# Revit family: vanity unit for handrinse basin, door hinge
name_source: partatom
category: Furniture
units: mm (PartAtom-declared; Revit-internal decimal feet)

## family parameters
Always vertical = Yes
Cut with Voids When Loaded = No
OmniClass Number = 23.45.00.00
OmniClass Title = Sanitary, Laundry, and Cleaning Equipment
Room Calculation Point = No
Shared = Yes
Work Plane-Based = No

## types (48) — shared parameters
BIMOBJECT = Sanitary: Compound units
CATALOG = Hansgrohe
DESIGN = Germany
ETIM = EC011381 | Bathroom furniture set
IFC = Furnishing element
L = 340
MASTERFORMAT = 12 35 30.23 | Bathroom Casework
Manufacturer = Hansgrohe
NBSYN = $BASENUMBER.-$ARTNR.-$OBERFLAECHE.-$SURFACE.-$LODLEVEL.
NN = Vanity Unit for handrinse basin, door hinge
OBJECTTYPE = Object (single object)
OMNICLASS = 23-21 19 15 33 13 | Residential Bathroom Specialty Casework
PRODUCTFAMILY = Xelu Q
PRODUCTGROUP = vanity unit
PRODUCTURL = https://pro.hansgrohe.com
REGIONSET = Worldwide
UNICLASS2015 = Pr_40_30_78_05 | Bathroom furniture
UNICLASS_2015_CODE = 40_30_78_05
UNIFORMATII = E2010 | Fixed Furnishings
UNSPSC = 56 | Furniture and Furnishings
WEIGHT = 9.9
etim7_EC011381 = EC011381

## per-type parameters (varying)
| type | ARTNR | BASENUMBER | GTINCODE | LINA | LODLEVEL | Model | NAME | NB | OBERFLAECHE | PERMALINK | SURFACE |
| Vanity unit 340_245 for handrinse basin, door hinge left-54011000-High Gloss White-CHROME-200 | 54011000 | Vanity unit 340/245 for handrinse basin, door hinge left | 4059625455135 | Vanity unit 340/245 for handrinse basin, door hinge left-54011000-High Gloss White-CHROME-200 | 200 | Vanity unit 340/245 for handrinse basin, door hinge left-54011000-High Gloss White-CHROME-200 | Xelu Q Vanity unit High Gloss White 340/245 for handrinse basin, door hinge left | Vanity unit 340/245 for handrinse basin, door hinge left-54011000-High Gloss White-CHROME-200 | High Gloss White | 54011XXX | CHROME |
| Vanity unit 340_245 for handrinse basin, door hinge left-54011000-High Gloss White-CHROME-400 | 54011000 | Vanity unit 340/245 for handrinse basin, door hinge left | 4059625455135 | Vanity unit 340/245 for handrinse basin, door hinge left-54011000-High Gloss White-CHROME-400 | 400 | Vanity unit 340/245 for handrinse basin, door hinge left-54011000-High Gloss White-CHROME-400 | Xelu Q Vanity unit High Gloss White 340/245 for handrinse basin, door hinge left | Vanity unit 340/245 for handrinse basin, door hinge left-54011000-High Gloss White-CHROME-400 | High Gloss White | 54011XXX | CHROME |
| Vanity unit 340_245 for handrinse basin, door hinge left-54011670-High Gloss White-MATT_BLACK-200 | 54011670 | Vanity unit 340/245 for handrinse basin, door hinge left | 4059625455135 | Vanity unit 340/245 for handrinse basin, door hinge left-54011670-High Gloss White-MATT_BLACK-200 | 200 | Vanity unit 340/245 for handrinse basin, door hinge left-54011670-High Gloss White-MATT_BLACK-200 | Xelu Q Vanity unit High Gloss White 340/245 for handrinse basin, door hinge left | Vanity unit 340/245 for handrinse basin, door hinge left-54011670-High Gloss White-MATT_BLACK-200 | High Gloss White | 54011XXX | MATT_BLACK |
| Vanity unit 340_245 for handrinse basin, door hinge left-54011670-High Gloss White-MATT_BLACK-400 | 54011670 | Vanity unit 340/245 for handrinse basin, door hinge left | 4059625455135 | Vanity unit 340/245 for handrinse basin, door hinge left-54011670-High Gloss White-MATT_BLACK-400 | 400 | Vanity unit 340/245 for handrinse basin, door hinge left-54011670-High Gloss White-MATT_BLACK-400 | Xelu Q Vanity unit High Gloss White 340/245 for handrinse basin, door hinge left | Vanity unit 340/245 for handrinse basin, door hinge left-54011670-High Gloss White-MATT_BLACK-400 | High Gloss White | 54011XXX | MATT_BLACK |
| Vanity unit 340_245 for handrinse basin, door hinge left-54011700-High Gloss White-MATT_WHITE-200 | 54011700 | Vanity unit 340/245 for handrinse basin, door hinge left | 4059625455135 | Vanity unit 340/245 for handrinse basin, door hinge left-54011700-High Gloss White-MATT_WHITE-200 | 200 | Vanity unit 340/245 for handrinse basin, door hinge left-54011700-High Gloss White-MATT_WHITE-200 | Xelu Q Vanity unit High Gloss White 340/245 for handrinse basin, door hinge left | Vanity unit 340/245 for handrinse basin, door hinge left-54011700-High Gloss White-MATT_WHITE-200 | High Gloss White | 54011XXX | MATT_WHITE |
| Vanity unit 340_245 for handrinse basin, door hinge left-54011700-High Gloss White-MATT_WHITE-400 | 54011700 | Vanity unit 340/245 for handrinse basin, door hinge left | 4059625455135 | Vanity unit 340/245 for handrinse basin, door hinge left-54011700-High Gloss White-MATT_WHITE-400 | 400 | Vanity unit 340/245 for handrinse basin, door hinge left-54011700-High Gloss White-MATT_WHITE-400 | Xelu Q Vanity unit High Gloss White 340/245 for handrinse basin, door hinge left | Vanity unit 340/245 for handrinse basin, door hinge left-54011700-High Gloss White-MATT_WHITE-400 | High Gloss White | 54011XXX | MATT_WHITE |
| Vanity unit 340_245 for handrinse basin, door hinge left-54012000-Diamond Matt Grey-CHROME-200 | 54012000 | Vanity unit 340/245 for handrinse basin, door hinge left | 4059625455104 | Vanity unit 340/245 for handrinse basin, door hinge left-54012000-Diamond Matt Grey-CHROME-200 | 200 | Vanity unit 340/245 for handrinse basin, door hinge left-54012000-Diamond Matt Grey-CHROME-200 | Xelu Q Vanity unit Diamond Matt Grey 340/245 for handrinse basin, door hinge left | Vanity unit 340/245 for handrinse basin, door hinge left-54012000-Diamond Matt Grey-CHROME-200 | Diamond Matt Grey | 54012XXX | CHROME |
| Vanity unit 340_245 for handrinse basin, door hinge left-54012000-Diamond Matt Grey-CHROME-400 | 54012000 | Vanity unit 340/245 for handrinse basin, door hinge left | 4059625455104 | Vanity unit 340/245 for handrinse basin, door hinge left-54012000-Diamond Matt Grey-CHROME-400 | 400 | Vanity unit 340/245 for handrinse basin, door hinge left-54012000-Diamond Matt Grey-CHROME-400 | Xelu Q Vanity unit Diamond Matt Grey 340/245 for handrinse basin, door hinge left | Vanity unit 340/245 for handrinse basin, door hinge left-54012000-Diamond Matt Grey-CHROME-400 | Diamond Matt Grey | 54012XXX | CHROME |
| Vanity unit 340_245 for handrinse basin, door hinge left-54012670-Diamond Matt Grey-MATT_BLACK-200 | 54012670 | Vanity unit 340/245 for handrinse basin, door hinge left | 4059625455104 | Vanity unit 340/245 for handrinse basin, door hinge left-54012670-Diamond Matt Grey-MATT_BLACK-200 | 200 | Vanity unit 340/245 for handrinse basin, door hinge left-54012670-Diamond Matt Grey-MATT_BLACK-200 | Xelu Q Vanity unit Diamond Matt Grey 340/245 for handrinse basin, door hinge left | Vanity unit 340/245 for handrinse basin, door hinge left-54012670-Diamond Matt Grey-MATT_BLACK-200 | Diamond Matt Grey | 54012XXX | MATT_BLACK |
| Vanity unit 340_245 for handrinse basin, door hinge left-54012670-Diamond Matt Grey-MATT_BLACK-400 | 54012670 | Vanity unit 340/245 for handrinse basin, door hinge left | 4059625455104 | Vanity unit 340/245 for handrinse basin, door hinge left-54012670-Diamond Matt Grey-MATT_BLACK-400 | 400 | Vanity unit 340/245 for handrinse basin, door hinge left-54012670-Diamond Matt Grey-MATT_BLACK-400 | Xelu Q Vanity unit Diamond Matt Grey 340/245 for handrinse basin, door hinge left | Vanity unit 340/245 for handrinse basin, door hinge left-54012670-Diamond Matt Grey-MATT_BLACK-400 | Diamond Matt Grey | 54012XXX | MATT_BLACK |
| Vanity unit 340_245 for handrinse basin, door hinge left-54012700-Diamond Matt Grey-MATT_WHITE-200 | 54012700 | Vanity unit 340/245 for handrinse basin, door hinge left | 4059625455104 | Vanity unit 340/245 for handrinse basin, door hinge left-54012700-Diamond Matt Grey-MATT_WHITE-200 | 200 | Vanity unit 340/245 for handrinse basin, door hinge left-54012700-Diamond Matt Grey-MATT_WHITE-200 | Xelu Q Vanity unit Diamond Matt Grey 340/245 for handrinse basin, door hinge left | Vanity unit 340/245 for handrinse basin, door hinge left-54012700-Diamond Matt Grey-MATT_WHITE-200 | Diamond Matt Grey | 54012XXX | MATT_WHITE |
| Vanity unit 340_245 for handrinse basin, door hinge left-54012700-Diamond Matt Grey-MATT_WHITE-400 | 54012700 | Vanity unit 340/245 for handrinse basin, door hinge left | 4059625455104 | Vanity unit 340/245 for handrinse basin, door hinge left-54012700-Diamond Matt Grey-MATT_WHITE-400 | 400 | Vanity unit 340/245 for handrinse basin, door hinge left-54012700-Diamond Matt Grey-MATT_WHITE-400 | Xelu Q Vanity unit Diamond Matt Grey 340/245 for handrinse basin, door hinge left | Vanity unit 340/245 for handrinse basin, door hinge left-54012700-Diamond Matt Grey-MATT_WHITE-400 | Diamond Matt Grey | 54012XXX | MATT_WHITE |
| Vanity unit 340_245 for handrinse basin, door hinge left-54013000-Natural Oak-CHROME-200 | 54013000 | Vanity unit 340/245 for handrinse basin, door hinge left | 4059625455074 | Vanity unit 340/245 for handrinse basin, door hinge left-54013000-Natural Oak-CHROME-200 | 200 | Vanity unit 340/245 for handrinse basin, door hinge left-54013000-Natural Oak-CHROME-200 | Xelu Q Vanity unit Natual Oak 340/245 for handrinse basin, door hinge left | Vanity unit 340/245 for handrinse basin, door hinge left-54013000-Natural Oak-CHROME-200 | Natural Oak | 54013XXX | CHROME |
| Vanity unit 340_245 for handrinse basin, door hinge left-54013000-Natural Oak-CHROME-400 | 54013000 | Vanity unit 340/245 for handrinse basin, door hinge left | 4059625455074 | Vanity unit 340/245 for handrinse basin, door hinge left-54013000-Natural Oak-CHROME-400 | 400 | Vanity unit 340/245 for handrinse basin, door hinge left-54013000-Natural Oak-CHROME-400 | Xelu Q Vanity unit Natual Oak 340/245 for handrinse basin, door hinge left | Vanity unit 340/245 for handrinse basin, door hinge left-54013000-Natural Oak-CHROME-400 | Natural Oak | 54013XXX | CHROME |
| Vanity unit 340_245 for handrinse basin, door hinge left-54013670-Natural Oak-MATT_BLACK-200 | 54013670 | Vanity unit 340/245 for handrinse basin, door hinge left | 4059625455074 | Vanity unit 340/245 for handrinse basin, door hinge left-54013670-Natural Oak-MATT_BLACK-200 | 200 | Vanity unit 340/245 for handrinse basin, door hinge left-54013670-Natural Oak-MATT_BLACK-200 | Xelu Q Vanity unit Natual Oak 340/245 for handrinse basin, door hinge left | Vanity unit 340/245 for handrinse basin, door hinge left-54013670-Natural Oak-MATT_BLACK-200 | Natural Oak | 54013XXX | MATT_BLACK |
| Vanity unit 340_245 for handrinse basin, door hinge left-54013670-Natural Oak-MATT_BLACK-400 | 54013670 | Vanity unit 340/245 for handrinse basin, door hinge left | 4059625455074 | Vanity unit 340/245 for handrinse basin, door hinge left-54013670-Natural Oak-MATT_BLACK-400 | 400 | Vanity unit 340/245 for handrinse basin, door hinge left-54013670-Natural Oak-MATT_BLACK-400 | Xelu Q Vanity unit Natual Oak 340/245 for handrinse basin, door hinge left | Vanity unit 340/245 for handrinse basin, door hinge left-54013670-Natural Oak-MATT_BLACK-400 | Natural Oak | 54013XXX | MATT_BLACK |
| Vanity unit 340_245 for handrinse basin, door hinge left-54013700-Natural Oak-MATT_WHITE-200 | 54013700 | Vanity unit 340/245 for handrinse basin, door hinge left | 4059625455074 | Vanity unit 340/245 for handrinse basin, door hinge left-54013700-Natural Oak-MATT_WHITE-200 | 200 | Vanity unit 340/245 for handrinse basin, door hinge left-54013700-Natural Oak-MATT_WHITE-200 | Xelu Q Vanity unit Natual Oak 340/245 for handrinse basin, door hinge left | Vanity unit 340/245 for handrinse basin, door hinge left-54013700-Natural Oak-MATT_WHITE-200 | Natural Oak | 54013XXX | MATT_WHITE |
| Vanity unit 340_245 for handrinse basin, door hinge left-54013700-Natural Oak-MATT_WHITE-400 | 54013700 | Vanity unit 340/245 for handrinse basin, door hinge left | 4059625455074 | Vanity unit 340/245 for handrinse basin, door hinge left-54013700-Natural Oak-MATT_WHITE-400 | 400 | Vanity unit 340/245 for handrinse basin, door hinge left-54013700-Natural Oak-MATT_WHITE-400 | Xelu Q Vanity unit Natual Oak 340/245 for handrinse basin, door hinge left | Vanity unit 340/245 for handrinse basin, door hinge left-54013700-Natural Oak-MATT_WHITE-400 | Natural Oak | 54013XXX | MATT_WHITE |
| Vanity unit 340_245 for handrinse basin, door hinge left-54014000-Dark Walnut-CHROME-200 | 54014000 | Vanity unit 340/245 for handrinse basin, door hinge left | 4059625455043 | Vanity unit 340/245 for handrinse basin, door hinge left-54014000-Dark Walnut-CHROME-200 | 200 | Vanity unit 340/245 for handrinse basin, door hinge left-54014000-Dark Walnut-CHROME-200 | Xelu Q Vanity unit Dark Walnut 340/245 for handrinse basin, door hinge left | Vanity unit 340/245 for handrinse basin, door hinge left-54014000-Dark Walnut-CHROME-200 | Dark Walnut | 54014XXX | CHROME |
| Vanity unit 340_245 for handrinse basin, door hinge left-54014000-Dark Walnut-CHROME-400 | 54014000 | Vanity unit 340/245 for handrinse basin, door hinge left | 4059625455043 | Vanity unit 340/245 for handrinse basin, door hinge left-54014000-Dark Walnut-CHROME-400 | 400 | Vanity unit 340/245 for handrinse basin, door hinge left-54014000-Dark Walnut-CHROME-400 | Xelu Q Vanity unit Dark Walnut 340/245 for handrinse basin, door hinge left | Vanity unit 340/245 for handrinse basin, door hinge left-54014000-Dark Walnut-CHROME-400 | Dark Walnut | 54014XXX | CHROME |
| Vanity unit 340_245 for handrinse basin, door hinge left-54014670-Dark Walnut-MATT_BLACK-200 | 54014670 | Vanity unit 340/245 for handrinse basin, door hinge left | 4059625455043 | Vanity unit 340/245 for handrinse basin, door hinge left-54014670-Dark Walnut-MATT_BLACK-200 | 200 | Vanity unit 340/245 for handrinse basin, door hinge left-54014670-Dark Walnut-MATT_BLACK-200 | Xelu Q Vanity unit Dark Walnut 340/245 for handrinse basin, door hinge left | Vanity unit 340/245 for handrinse basin, door hinge left-54014670-Dark Walnut-MATT_BLACK-200 | Dark Walnut | 54014XXX | MATT_BLACK |
| Vanity unit 340_245 for handrinse basin, door hinge left-54014670-Dark Walnut-MATT_BLACK-400 | 54014670 | Vanity unit 340/245 for handrinse basin, door hinge left | 4059625455043 | Vanity unit 340/245 for handrinse basin, door hinge left-54014670-Dark Walnut-MATT_BLACK-400 | 400 | Vanity unit 340/245 for handrinse basin, door hinge left-54014670-Dark Walnut-MATT_BLACK-400 | Xelu Q Vanity unit Dark Walnut 340/245 for handrinse basin, door hinge left | Vanity unit 340/245 for handrinse basin, door hinge left-54014670-Dark Walnut-MATT_BLACK-400 | Dark Walnut | 54014XXX | MATT_BLACK |
| Vanity unit 340_245 for handrinse basin, door hinge left-54014700-Dark Walnut-MATT_WHITE-200 | 54014700 | Vanity unit 340/245 for handrinse basin, door hinge left | 4059625455043 | Vanity unit 340/245 for handrinse basin, door hinge left-54014700-Dark Walnut-MATT_WHITE-200 | 200 | Vanity unit 340/245 for handrinse basin, door hinge left-54014700-Dark Walnut-MATT_WHITE-200 | Xelu Q Vanity unit Dark Walnut 340/245 for handrinse basin, door hinge left | Vanity unit 340/245 for handrinse basin, door hinge left-54014700-Dark Walnut-MATT_WHITE-200 | Dark Walnut | 54014XXX | MATT_WHITE |
| Vanity unit 340_245 for handrinse basin, door hinge left-54014700-Dark Walnut-MATT_WHITE-400 | 54014700 | Vanity unit 340/245 for handrinse basin, door hinge left | 4059625455043 | Vanity unit 340/245 for handrinse basin, door hinge left-54014700-Dark Walnut-MATT_WHITE-400 | 400 | Vanity unit 340/245 for handrinse basin, door hinge left-54014700-Dark Walnut-MATT_WHITE-400 | Xelu Q Vanity unit Dark Walnut 340/245 for handrinse basin, door hinge left | Vanity unit 340/245 for handrinse basin, door hinge left-54014700-Dark Walnut-MATT_WHITE-400 | Dark Walnut | 54014XXX | MATT_WHITE |
| Vanity unit 340_245 for handrinse basin, door hinge right-54015000-High Gloss White-CHROME-200 | 54015000 | Vanity unit 340/245 for handrinse basin, door hinge right | 4059625455012 | Vanity unit 340/245 for handrinse basin, door hinge right-54015000-High Gloss White-CHROME-200 | 200 | Vanity unit 340/245 for handrinse basin, door hinge right-54015000-High Gloss White-CHROME-200 | Xelu Q Vanity unit High Gloss White 340/245 for handrinse basin, door hinge right | Vanity unit 340/245 for handrinse basin, door hinge right-54015000-High Gloss White-CHROME-200 | High Gloss White | 54015XXX | CHROME |
| Vanity unit 340_245 for handrinse basin, door hinge right-54015000-High Gloss White-CHROME-400 | 54015000 | Vanity unit 340/245 for handrinse basin, door hinge right | 4059625455012 | Vanity unit 340/245 for handrinse basin, door hinge right-54015000-High Gloss White-CHROME-400 | 400 | Vanity unit 340/245 for handrinse basin, door hinge right-54015000-High Gloss White-CHROME-400 | Xelu Q Vanity unit High Gloss White 340/245 for handrinse basin, door hinge right | Vanity unit 340/245 for handrinse basin, door hinge right-54015000-High Gloss White-CHROME-400 | High Gloss White | 54015XXX | CHROME |
| Vanity unit 340_245 for handrinse basin, door hinge right-54015670-High Gloss White-MATT_BLACK-200 | 54015670 | Vanity unit 340/245 for handrinse basin, door hinge right | 4059625455012 | Vanity unit 340/245 for handrinse basin, door hinge right-54015670-High Gloss White-MATT_BLACK-200 | 200 | Vanity unit 340/245 for handrinse basin, door hinge right-54015670-High Gloss White-MATT_BLACK-200 | Xelu Q Vanity unit High Gloss White 340/245 for handrinse basin, door hinge right | Vanity unit 340/245 for handrinse basin, door hinge right-54015670-High Gloss White-MATT_BLACK-200 | High Gloss White | 54015XXX | MATT_BLACK |
| Vanity unit 340_245 for handrinse basin, door hinge right-54015670-High Gloss White-MATT_BLACK-400 | 54015670 | Vanity unit 340/245 for handrinse basin, door hinge right | 4059625455012 | Vanity unit 340/245 for handrinse basin, door hinge right-54015670-High Gloss White-MATT_BLACK-400 | 400 | Vanity unit 340/245 for handrinse basin, door hinge right-54015670-High Gloss White-MATT_BLACK-400 | Xelu Q Vanity unit High Gloss White 340/245 for handrinse basin, door hinge right | Vanity unit 340/245 for handrinse basin, door hinge right-54015670-High Gloss White-MATT_BLACK-400 | High Gloss White | 54015XXX | MATT_BLACK |
| Vanity unit 340_245 for handrinse basin, door hinge right-54015700-High Gloss White-MATT_WHITE-200 | 54015700 | Vanity unit 340/245 for handrinse basin, door hinge right | 4059625455012 | Vanity unit 340/245 for handrinse basin, door hinge right-54015700-High Gloss White-MATT_WHITE-200 | 200 | Vanity unit 340/245 for handrinse basin, door hinge right-54015700-High Gloss White-MATT_WHITE-200 | Xelu Q Vanity unit High Gloss White 340/245 for handrinse basin, door hinge right | Vanity unit 340/245 for handrinse basin, door hinge right-54015700-High Gloss White-MATT_WHITE-200 | High Gloss White | 54015XXX | MATT_WHITE |
| Vanity unit 340_245 for handrinse basin, door hinge right-54015700-High Gloss White-MATT_WHITE-400 | 54015700 | Vanity unit 340/245 for handrinse basin, door hinge right | 4059625455012 | Vanity unit 340/245 for handrinse basin, door hinge right-54015700-High Gloss White-MATT_WHITE-400 | 400 | Vanity unit 340/245 for handrinse basin, door hinge right-54015700-High Gloss White-MATT_WHITE-400 | Xelu Q Vanity unit High Gloss White 340/245 for handrinse basin, door hinge right | Vanity unit 340/245 for handrinse basin, door hinge right-54015700-High Gloss White-MATT_WHITE-400 | High Gloss White | 54015XXX | MATT_WHITE |
| Vanity unit 340_245 for handrinse basin, door hinge right-54016000-Diamond Matt Grey-CHROME-200 | 54016000 | Vanity unit 340/245 for handrinse basin, door hinge right | 4059625454886 | Vanity unit 340/245 for handrinse basin, door hinge right-54016000-Diamond Matt Grey-CHROME-200 | 200 | Vanity unit 340/245 for handrinse basin, door hinge right-54016000-Diamond Matt Grey-CHROME-200 | Xelu Q Vanity unit Diamond Matt Grey 340/245 for handrinse basin, door hinge right | Vanity unit 340/245 for handrinse basin, door hinge right-54016000-Diamond Matt Grey-CHROME-200 | Diamond Matt Grey | 54016XXX | CHROME |
| Vanity unit 340_245 for handrinse basin, door hinge right-54016000-Diamond Matt Grey-CHROME-400 | 54016000 | Vanity unit 340/245 for handrinse basin, door hinge right | 4059625454886 | Vanity unit 340/245 for handrinse basin, door hinge right-54016000-Diamond Matt Grey-CHROME-400 | 400 | Vanity unit 340/245 for handrinse basin, door hinge right-54016000-Diamond Matt Grey-CHROME-400 | Xelu Q Vanity unit Diamond Matt Grey 340/245 for handrinse basin, door hinge right | Vanity unit 340/245 for handrinse basin, door hinge right-54016000-Diamond Matt Grey-CHROME-400 | Diamond Matt Grey | 54016XXX | CHROME |
| Vanity unit 340_245 for handrinse basin, door hinge right-54016670-Diamond Matt Grey-MATT_BLACK-200 | 54016670 | Vanity unit 340/245 for handrinse basin, door hinge right | 4059625454886 | Vanity unit 340/245 for handrinse basin, door hinge right-54016670-Diamond Matt Grey-MATT_BLACK-200 | 200 | Vanity unit 340/245 for handrinse basin, door hinge right-54016670-Diamond Matt Grey-MATT_BLACK-200 | Xelu Q Vanity unit Diamond Matt Grey 340/245 for handrinse basin, door hinge right | Vanity unit 340/245 for handrinse basin, door hinge right-54016670-Diamond Matt Grey-MATT_BLACK-200 | Diamond Matt Grey | 54016XXX | MATT_BLACK |
| Vanity unit 340_245 for handrinse basin, door hinge right-54016670-Diamond Matt Grey-MATT_BLACK-400 | 54016670 | Vanity unit 340/245 for handrinse basin, door hinge right | 4059625454886 | Vanity unit 340/245 for handrinse basin, door hinge right-54016670-Diamond Matt Grey-MATT_BLACK-400 | 400 | Vanity unit 340/245 for handrinse basin, door hinge right-54016670-Diamond Matt Grey-MATT_BLACK-400 | Xelu Q Vanity unit Diamond Matt Grey 340/245 for handrinse basin, door hinge right | Vanity unit 340/245 for handrinse basin, door hinge right-54016670-Diamond Matt Grey-MATT_BLACK-400 | Diamond Matt Grey | 54016XXX | MATT_BLACK |
| Vanity unit 340_245 for handrinse basin, door hinge right-54016700-Diamond Matt Grey-MATT_WHITE-200 | 54016700 | Vanity unit 340/245 for handrinse basin, door hinge right | 4059625454886 | Vanity unit 340/245 for handrinse basin, door hinge right-54016700-Diamond Matt Grey-MATT_WHITE-200 | 200 | Vanity unit 340/245 for handrinse basin, door hinge right-54016700-Diamond Matt Grey-MATT_WHITE-200 | Xelu Q Vanity unit Diamond Matt Grey 340/245 for handrinse basin, door hinge right | Vanity unit 340/245 for handrinse basin, door hinge right-54016700-Diamond Matt Grey-MATT_WHITE-200 | Diamond Matt Grey | 54016XXX | MATT_WHITE |
| Vanity unit 340_245 for handrinse basin, door hinge right-54016700-Diamond Matt Grey-MATT_WHITE-400 | 54016700 | Vanity unit 340/245 for handrinse basin, door hinge right | 4059625454886 | Vanity unit 340/245 for handrinse basin, door hinge right-54016700-Diamond Matt Grey-MATT_WHITE-400 | 400 | Vanity unit 340/245 for handrinse basin, door hinge right-54016700-Diamond Matt Grey-MATT_WHITE-400 | Xelu Q Vanity unit Diamond Matt Grey 340/245 for handrinse basin, door hinge right | Vanity unit 340/245 for handrinse basin, door hinge right-54016700-Diamond Matt Grey-MATT_WHITE-400 | Diamond Matt Grey | 54016XXX | MATT_WHITE |
| Vanity unit 340_245 for handrinse basin, door hinge right-54017000-Natural Oak-CHROME-200 | 54017000 | Vanity unit 340/245 for handrinse basin, door hinge right | 4059625454855 | Vanity unit 340/245 for handrinse basin, door hinge right-54017000-Natural Oak-CHROME-200 | 200 | Vanity unit 340/245 for handrinse basin, door hinge right-54017000-Natural Oak-CHROME-200 | Xelu Q Vanity unit Natual Oak 340/245 for handrinse basin, door hinge right | Vanity unit 340/245 for handrinse basin, door hinge right-54017000-Natural Oak-CHROME-200 | Natural Oak | 54017XXX | CHROME |
| Vanity unit 340_245 for handrinse basin, door hinge right-54017000-Natural Oak-CHROME-400 | 54017000 | Vanity unit 340/245 for handrinse basin, door hinge right | 4059625454855 | Vanity unit 340/245 for handrinse basin, door hinge right-54017000-Natural Oak-CHROME-400 | 400 | Vanity unit 340/245 for handrinse basin, door hinge right-54017000-Natural Oak-CHROME-400 | Xelu Q Vanity unit Natual Oak 340/245 for handrinse basin, door hinge right | Vanity unit 340/245 for handrinse basin, door hinge right-54017000-Natural Oak-CHROME-400 | Natural Oak | 54017XXX | CHROME |
| Vanity unit 340_245 for handrinse basin, door hinge right-54017670-Natural Oak-MATT_BLACK-200 | 54017670 | Vanity unit 340/245 for handrinse basin, door hinge right | 4059625454855 | Vanity unit 340/245 for handrinse basin, door hinge right-54017670-Natural Oak-MATT_BLACK-200 | 200 | Vanity unit 340/245 for handrinse basin, door hinge right-54017670-Natural Oak-MATT_BLACK-200 | Xelu Q Vanity unit Natual Oak 340/245 for handrinse basin, door hinge right | Vanity unit 340/245 for handrinse basin, door hinge right-54017670-Natural Oak-MATT_BLACK-200 | Natural Oak | 54017XXX | MATT_BLACK |
| Vanity unit 340_245 for handrinse basin, door hinge right-54017670-Natural Oak-MATT_BLACK-400 | 54017670 | Vanity unit 340/245 for handrinse basin, door hinge right | 4059625454855 | Vanity unit 340/245 for handrinse basin, door hinge right-54017670-Natural Oak-MATT_BLACK-400 | 400 | Vanity unit 340/245 for handrinse basin, door hinge right-54017670-Natural Oak-MATT_BLACK-400 | Xelu Q Vanity unit Natual Oak 340/245 for handrinse basin, door hinge right | Vanity unit 340/245 for handrinse basin, door hinge right-54017670-Natural Oak-MATT_BLACK-400 | Natural Oak | 54017XXX | MATT_BLACK |
| Vanity unit 340_245 for handrinse basin, door hinge right-54017700-Natural Oak-MATT_WHITE-200 | 54017700 | Vanity unit 340/245 for handrinse basin, door hinge right | 4059625454855 | Vanity unit 340/245 for handrinse basin, door hinge right-54017700-Natural Oak-MATT_WHITE-200 | 200 | Vanity unit 340/245 for handrinse basin, door hinge right-54017700-Natural Oak-MATT_WHITE-200 | Xelu Q Vanity unit Natual Oak 340/245 for handrinse basin, door hinge right | Vanity unit 340/245 for handrinse basin, door hinge right-54017700-Natural Oak-MATT_WHITE-200 | Natural Oak | 54017XXX | MATT_WHITE |
| Vanity unit 340_245 for handrinse basin, door hinge right-54017700-Natural Oak-MATT_WHITE-400 | 54017700 | Vanity unit 340/245 for handrinse basin, door hinge right | 4059625454855 | Vanity unit 340/245 for handrinse basin, door hinge right-54017700-Natural Oak-MATT_WHITE-400 | 400 | Vanity unit 340/245 for handrinse basin, door hinge right-54017700-Natural Oak-MATT_WHITE-400 | Xelu Q Vanity unit Natual Oak 340/245 for handrinse basin, door hinge right | Vanity unit 340/245 for handrinse basin, door hinge right-54017700-Natural Oak-MATT_WHITE-400 | Natural Oak | 54017XXX | MATT_WHITE |
| Vanity unit 340_245 for handrinse basin, door hinge right-54018000-Dark Walnut-CHROME-200 | 54018000 | Vanity unit 340/245 for handrinse basin, door hinge right | 4059625455319 | Vanity unit 340/245 for handrinse basin, door hinge right-54018000-Dark Walnut-CHROME-200 | 200 | Vanity unit 340/245 for handrinse basin, door hinge right-54018000-Dark Walnut-CHROME-200 | Xelu Q Vanity unit Dark Walnut 340/245 for handrinse basin, door hinge right | Vanity unit 340/245 for handrinse basin, door hinge right-54018000-Dark Walnut-CHROME-200 | Dark Walnut | 54018XXX | CHROME |
| Vanity unit 340_245 for handrinse basin, door hinge right-54018000-Dark Walnut-CHROME-400 | 54018000 | Vanity unit 340/245 for handrinse basin, door hinge right | 4059625455319 | Vanity unit 340/245 for handrinse basin, door hinge right-54018000-Dark Walnut-CHROME-400 | 400 | Vanity unit 340/245 for handrinse basin, door hinge right-54018000-Dark Walnut-CHROME-400 | Xelu Q Vanity unit Dark Walnut 340/245 for handrinse basin, door hinge right | Vanity unit 340/245 for handrinse basin, door hinge right-54018000-Dark Walnut-CHROME-400 | Dark Walnut | 54018XXX | CHROME |
| Vanity unit 340_245 for handrinse basin, door hinge right-54018670-Dark Walnut-MATT_BLACK-200 | 54018670 | Vanity unit 340/245 for handrinse basin, door hinge right | 4059625455319 | Vanity unit 340/245 for handrinse basin, door hinge right-54018670-Dark Walnut-MATT_BLACK-200 | 200 | Vanity unit 340/245 for handrinse basin, door hinge right-54018670-Dark Walnut-MATT_BLACK-200 | Xelu Q Vanity unit Dark Walnut 340/245 for handrinse basin, door hinge right | Vanity unit 340/245 for handrinse basin, door hinge right-54018670-Dark Walnut-MATT_BLACK-200 | Dark Walnut | 54018XXX | MATT_BLACK |
| Vanity unit 340_245 for handrinse basin, door hinge right-54018670-Dark Walnut-MATT_BLACK-400 | 54018670 | Vanity unit 340/245 for handrinse basin, door hinge right | 4059625455319 | Vanity unit 340/245 for handrinse basin, door hinge right-54018670-Dark Walnut-MATT_BLACK-400 | 400 | Vanity unit 340/245 for handrinse basin, door hinge right-54018670-Dark Walnut-MATT_BLACK-400 | Xelu Q Vanity unit Dark Walnut 340/245 for handrinse basin, door hinge right | Vanity unit 340/245 for handrinse basin, door hinge right-54018670-Dark Walnut-MATT_BLACK-400 | Dark Walnut | 54018XXX | MATT_BLACK |
| Vanity unit 340_245 for handrinse basin, door hinge right-54018700-Dark Walnut-MATT_WHITE-200 | 54018700 | Vanity unit 340/245 for handrinse basin, door hinge right | 4059625455319 | Vanity unit 340/245 for handrinse basin, door hinge right-54018700-Dark Walnut-MATT_WHITE-200 | 200 | Vanity unit 340/245 for handrinse basin, door hinge right-54018700-Dark Walnut-MATT_WHITE-200 | Xelu Q Vanity unit Dark Walnut 340/245 for handrinse basin, door hinge right | Vanity unit 340/245 for handrinse basin, door hinge right-54018700-Dark Walnut-MATT_WHITE-200 | Dark Walnut | 54018XXX | MATT_WHITE |
| Vanity unit 340_245 for handrinse basin, door hinge right-54018700-Dark Walnut-MATT_WHITE-400 | 54018700 | Vanity unit 340/245 for handrinse basin, door hinge right | 4059625455319 | Vanity unit 340/245 for handrinse basin, door hinge right-54018700-Dark Walnut-MATT_WHITE-400 | 400 | Vanity unit 340/245 for handrinse basin, door hinge right-54018700-Dark Walnut-MATT_WHITE-400 | Xelu Q Vanity unit Dark Walnut 340/245 for handrinse basin, door hinge right | Vanity unit 340/245 for handrinse basin, door hinge right-54018700-Dark Walnut-MATT_WHITE-400 | Dark Walnut | 54018XXX | MATT_WHITE |

type visibility flags: 48 boolean params named "<type name>_RX0RY0RZ0TX0TY0TZ0_V" — each type sets only its own to Yes (folded from table)

## geometry (parser evidence)
native form markers: Sweep x119
no freeform markers — native parametric forms only
